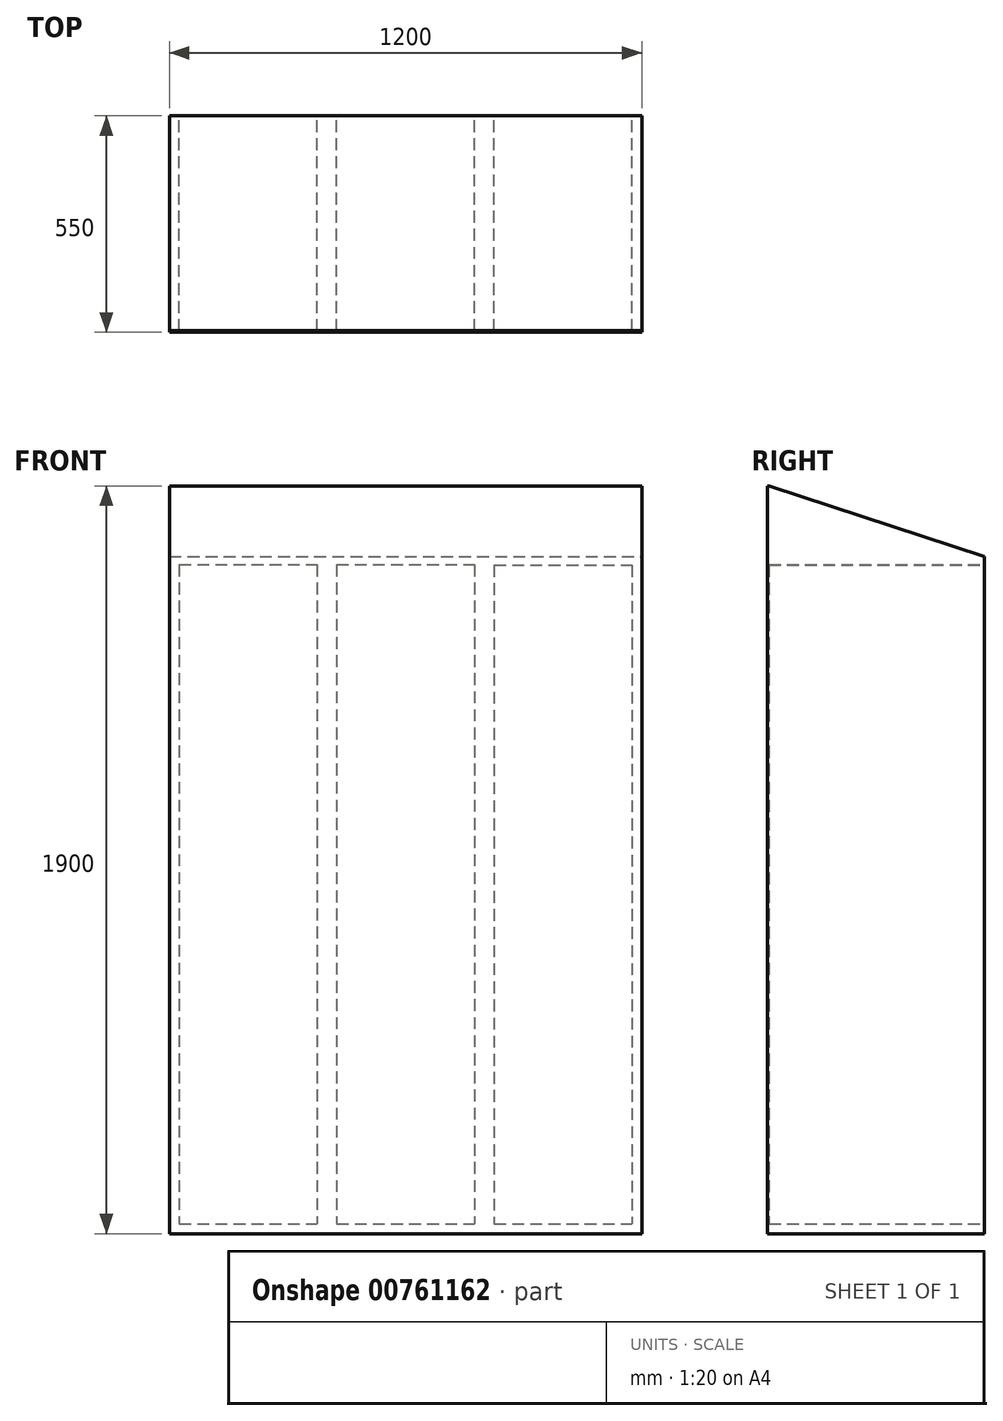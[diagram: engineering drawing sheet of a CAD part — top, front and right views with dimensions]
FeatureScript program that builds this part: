
annotation { "Feature Type Name" : "Feature", "Feature Type Description" : "" }
export const myFeature = defineFeature(function(context is Context, id is Id, definition is map)
    precondition{}
    {
        {
            var Q0;
            Q0=qCreatedBy(makeId("Front.planeOp"),FACE);
            var sketch = newSketch(context, id + "F0", { "sketchPlane" : qUnion([Q0])});
            skLineSegment(sketch, "E0.bottom", {"start": v(-1175, 1875) * mm, "end": v(25, 1875) * mm});
            skLineSegment(sketch, "E0.top", {"start": v(-1175, -25) * mm, "end": v(25, -25) * mm});
            skLineSegment(sketch, "E0.left", {"start": v(-1175, 1875) * mm, "end": v(-1175, -25) * mm});
            skLineSegment(sketch, "E0.right", {"start": v(25, 1875) * mm, "end": v(25, -25) * mm});
            skLineSegment(sketch, "E1.bottom", {"start": v(-1150, 1675) * mm, "end": v(-800, 1675) * mm});
            skLineSegment(sketch, "E1.top", {"start": v(-1150, 0) * mm, "end": v(-800, 0) * mm});
            skLineSegment(sketch, "E1.left", {"start": v(-1150, 1675) * mm, "end": v(-1150, 0) * mm});
            skLineSegment(sketch, "E1.right", {"start": v(-800, 1675) * mm, "end": v(-800, 0) * mm});
            skLineSegment(sketch, "E2.bottom", {"start": v(-750, 1675) * mm, "end": v(-400, 1675) * mm});
            skLineSegment(sketch, "E2.top", {"start": v(-750, 0) * mm, "end": v(-400, 0) * mm});
            skLineSegment(sketch, "E2.left", {"start": v(-750, 1675) * mm, "end": v(-750, 0) * mm});
            skLineSegment(sketch, "E2.right", {"start": v(-400, 1675) * mm, "end": v(-400, 0) * mm});
            skLineSegment(sketch, "E3.bottom", {"start": v(-350, 1673.74) * mm, "end": v(0, 1673.74) * mm});
            skLineSegment(sketch, "E3.top", {"start": v(-350, 0) * mm, "end": v(0, 0) * mm});
            skLineSegment(sketch, "E3.left", {"start": v(-350, 1673.74) * mm, "end": v(-350, 0) * mm});
            skLineSegment(sketch, "E3.right", {"start": v(0, 1673.74) * mm, "end": v(0, 0) * mm});
            skSolve(sketch);
        }
        {
            var Q0;
            Q0=makeQuery(id+"F0.imprint","IMPRINT",FACE,{"disambiguationData":[TD([[makeQuery(id+"F0.imprint","IMPRINT",EDGE,{"derivedFrom":sQuery(id+"F0.wireOp",EDGE,"E0.bottom")}),-1.0]])]});
            extrude(context, id + "F1", {"entities" : qUnion([Q0]), "depth" : 550 * mm, "offsetDistance" : 25 * mm});
        }
        {
            var Q0;
            Q0=makeQuery(id+"F1.opExtrude","CAP_EDGE",EDGE,{"disambiguationData":[OSD([sQuery(id+"F0.wireOp",EDGE,"E0.bottom")])],"isStart":true});
            chamfer(context, id + "F2", {"entities" : qUnion([Q0]), "chamferType" : ChamferType.TWO_OFFSETS, "width1" : 180 * mm, "oppositeDirection" : false, "width2" : 545 * mm, "tangentPropagation" : true});
        }
        {
            var Q0;
            Q0=makeQuery(id+"F0.imprint","IMPRINT",FACE,{"disambiguationData":[TD([[makeQuery(id+"F0.imprint","IMPRINT",EDGE,{"derivedFrom":sQuery(id+"F0.wireOp",EDGE,"E1.bottom")}),-1.0]])]});
            var Q1;
            Q1=makeQuery(id+"F0.imprint","IMPRINT",FACE,{"disambiguationData":[TD([[makeQuery(id+"F0.imprint","IMPRINT",EDGE,{"derivedFrom":sQuery(id+"F0.wireOp",EDGE,"E2.bottom")}),-1.0]])]});
            var Q2;
            Q2=makeQuery(id+"F0.imprint","IMPRINT",FACE,{"disambiguationData":[TD([[makeQuery(id+"F0.imprint","IMPRINT",EDGE,{"derivedFrom":sQuery(id+"F0.wireOp",EDGE,"E3.bottom")}),-1.0]])]});
            var Q3;
            Q3=makeQuery(id+"F0.imprint","IMPRINT",FACE,{"disambiguationData":[TD([[makeQuery(id+"F0.imprint","IMPRINT",EDGE,{"derivedFrom":sQuery(id+"F0.wireOp",EDGE,"E0.bottom")}),-1.0]])]});
            extrude(context, id + "F3", {"entities" : qUnion([Q0, Q1, Q2, Q3]), "operationType" : NewBodyOperationType.ADD, "depth" : 550 * mm, "offsetDistance" : 25 * mm, "hasSecondDirection" : true, "secondDirectionOppositeDirection" : false, "secondDirectionDepth" : 547 * mm});
        }
    });
